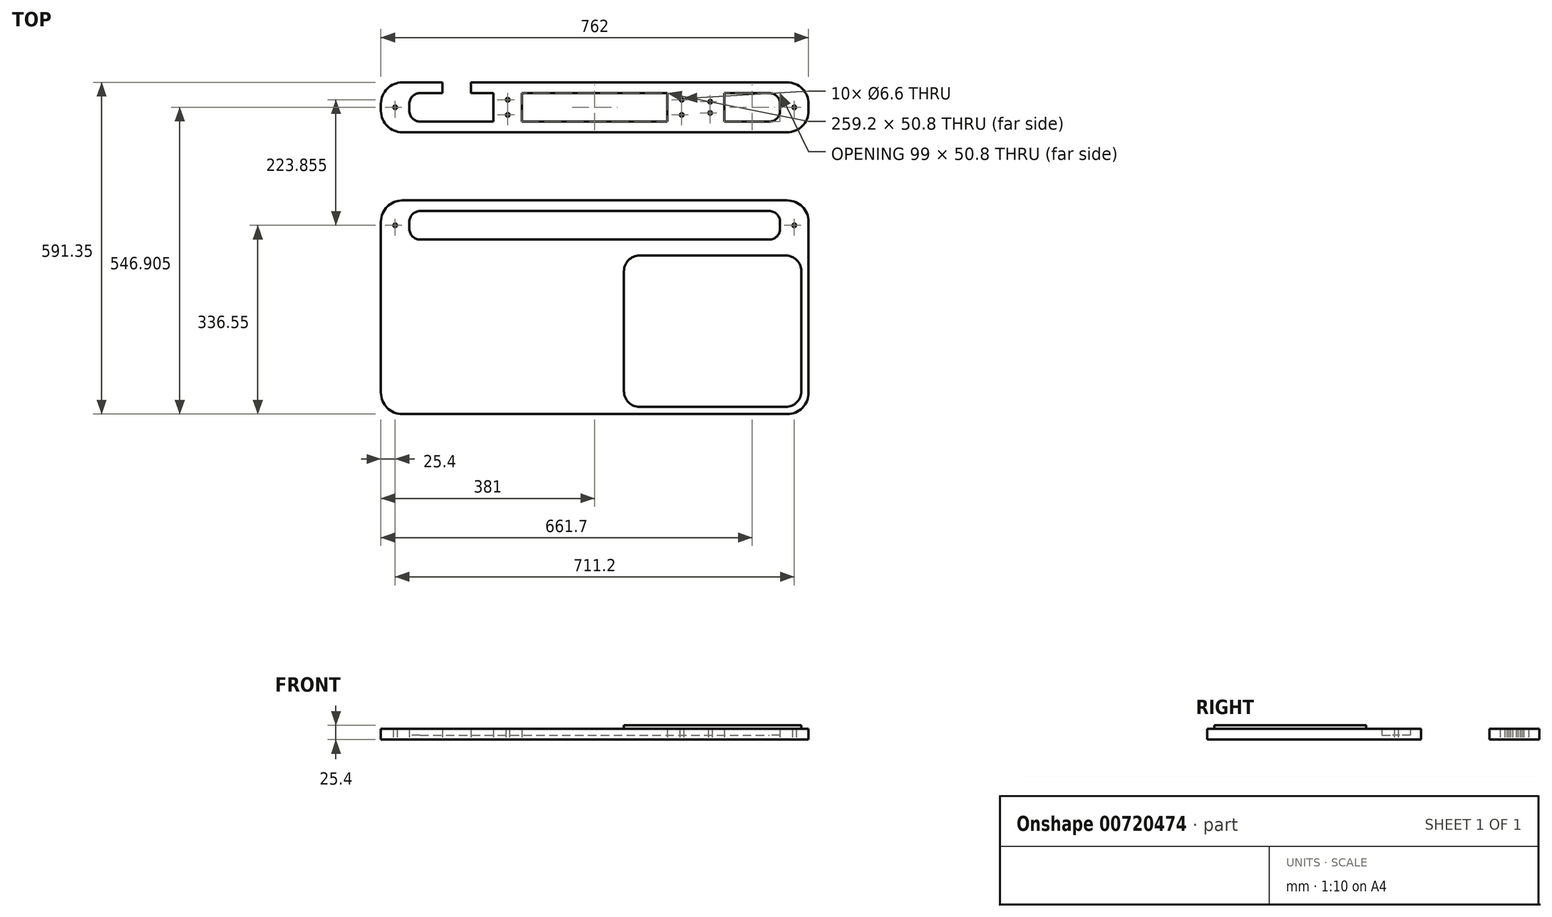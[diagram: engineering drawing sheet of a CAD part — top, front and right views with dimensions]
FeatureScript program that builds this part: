
annotation { "Feature Type Name" : "Feature", "Feature Type Description" : "" }
export const myFeature = defineFeature(function(context is Context, id is Id, definition is map)
    precondition{}
    {
        {
            var Q0;
            Q0=qCreatedBy(makeId("Top.planeOp"),FACE);
            var sketch = newSketch(context, id + "F0", { "sketchPlane" : qUnion([Q0])});
            skLineSegment(sketch, "E0.bottom", {"start": v(342.9, -190.5) * mm, "end": v(-342.9, -190.5) * mm});
            skLineSegment(sketch, "E0.top", {"start": v(342.9, 190.5) * mm, "end": v(-342.9, 190.5) * mm});
            skLineSegment(sketch, "E0.left", {"start": v(381, -152.4) * mm, "end": v(381, 152.4) * mm});
            skLineSegment(sketch, "E0.right", {"start": v(-381, -152.4) * mm, "end": v(-381, 152.4) * mm});
            skPoint(sketch, "E0.middle", {"position": v(0, 0) * mm});
            skLineSegment(sketch, "E1.bottom", {"start": v(340.3, -177.8) * mm, "end": v(80.07, -177.8) * mm});
            skLineSegment(sketch, "E1.top", {"start": v(340.3, 92.2) * mm, "end": v(80.07, 92.2) * mm});
            skLineSegment(sketch, "E1.left", {"start": v(368.3, -149.8) * mm, "end": v(368.3, 64.2) * mm});
            skLineSegment(sketch, "E1.right", {"start": v(52.07, -149.8) * mm, "end": v(52.07, 64.2) * mm});
            skPoint(sketch, "E1.middle", {"position": v(210.19, -42.8) * mm});
            skPoint(sketch, "E2.visualSharp", {"position": v(52.07, 92.2) * mm});
            skArc(sketch, "E2.filletArc", {"start": v(80.07, 92.2) * mm, "mid": v(60.27, 84) * mm, "end": v(52.07, 64.2) * mm});
            skPoint(sketch, "E3.visualSharp", {"position": v(368.3, 92.2) * mm});
            skArc(sketch, "E3.filletArc", {"start": v(368.3, 64.2) * mm, "mid": v(360.1, 84) * mm, "end": v(340.3, 92.2) * mm});
            skPoint(sketch, "E4.visualSharp", {"position": v(368.3, -177.8) * mm});
            skArc(sketch, "E4.filletArc", {"start": v(340.3, -177.8) * mm, "mid": v(360.1, -169.6) * mm, "end": v(368.3, -149.8) * mm});
            skPoint(sketch, "E5.visualSharp", {"position": v(52.07, -177.8) * mm});
            skArc(sketch, "E5.filletArc", {"start": v(52.07, -149.8) * mm, "mid": v(60.27, -169.6) * mm, "end": v(80.07, -177.8) * mm});
            skPoint(sketch, "E6.visualSharp", {"position": v(-381, 190.5) * mm});
            skArc(sketch, "E6.filletArc", {"start": v(-342.9, 190.5) * mm, "mid": v(-369.84, 179.34) * mm, "end": v(-381, 152.4) * mm});
            skPoint(sketch, "E7.visualSharp", {"position": v(-381, -190.5) * mm});
            skArc(sketch, "E7.filletArc", {"start": v(-381, -152.4) * mm, "mid": v(-369.84, -179.34) * mm, "end": v(-342.9, -190.5) * mm});
            skPoint(sketch, "E8.visualSharp", {"position": v(381, 190.5) * mm});
            skArc(sketch, "E8.filletArc", {"start": v(381, 152.4) * mm, "mid": v(369.84, 179.34) * mm, "end": v(342.9, 190.5) * mm});
            skPoint(sketch, "E9.visualSharp", {"position": v(381, -190.5) * mm});
            skArc(sketch, "E9.filletArc", {"start": v(342.9, -190.5) * mm, "mid": v(369.84, -179.34) * mm, "end": v(381, -152.4) * mm});
            skLineSegment(sketch, "E10", {"start": v(-342.9, 311.95) * mm, "end": v(342.9, 311.95) * mm});
            skLineSegment(sketch, "E11", {"start": v(381, 350.05) * mm, "end": v(381, 362.75) * mm});
            skLineSegment(sketch, "E12", {"start": v(-381, 350.05) * mm, "end": v(-381, 362.75) * mm});
            skLineSegment(sketch, "E13", {"start": v(-342.9, 400.85) * mm, "end": v(342.9, 400.85) * mm});
            skPoint(sketch, "E14.visualSharp", {"position": v(-381, 400.85) * mm});
            skArc(sketch, "E14.filletArc", {"start": v(-342.9, 400.85) * mm, "mid": v(-369.84, 389.7) * mm, "end": v(-381, 362.75) * mm});
            skPoint(sketch, "E15.visualSharp", {"position": v(381, 400.85) * mm});
            skArc(sketch, "E15.filletArc", {"start": v(381, 362.75) * mm, "mid": v(369.84, 389.7) * mm, "end": v(342.9, 400.85) * mm});
            skPoint(sketch, "E16.visualSharp", {"position": v(-381, 311.95) * mm});
            skArc(sketch, "E16.filletArc", {"start": v(-381, 350.05) * mm, "mid": v(-369.84, 323.11) * mm, "end": v(-342.9, 311.95) * mm});
            skPoint(sketch, "E17.visualSharp", {"position": v(381, 311.95) * mm});
            skArc(sketch, "E17.filletArc", {"start": v(342.9, 311.95) * mm, "mid": v(369.84, 323.11) * mm, "end": v(381, 350.05) * mm});
            skCircle(sketch, "E18", {"center": v(-355.6, 356.4) * mm, "radius": 3.3 * mm});
            skPoint(sketch, "E18.centerSnap0", {"position": v(-381, 356.4) * mm});
            skCircle(sketch, "E19", {"center": v(355.6, 356.4) * mm, "radius": 3.3 * mm});
            skPoint(sketch, "E19.centerSnap0", {"position": v(381, 356.4) * mm});
            skCircle(sketch, "E20", {"center": v(-355.6, 146.05) * mm, "radius": 3.3 * mm});
            skCircle(sketch, "E21", {"center": v(355.6, 146.05) * mm, "radius": 3.3 * mm});
            skLineSegment(sketch, "E22.bottom", {"start": v(-311.15, 171.45) * mm, "end": v(311.15, 171.45) * mm});
            skLineSegment(sketch, "E22.top", {"start": v(-311.15, 120.65) * mm, "end": v(311.15, 120.65) * mm});
            skLineSegment(sketch, "E22.left", {"start": v(-330.2, 152.4) * mm, "end": v(-330.2, 139.7) * mm});
            skLineSegment(sketch, "E22.right", {"start": v(330.2, 152.4) * mm, "end": v(330.2, 139.7) * mm});
            skPoint(sketch, "E23.visualSharp", {"position": v(-330.2, 381.8) * mm});
            skPoint(sketch, "E24.visualSharp", {"position": v(-330.2, 331) * mm});
            skPoint(sketch, "E25.visualSharp", {"position": v(330.2, 331) * mm});
            skPoint(sketch, "E26.visualSharp", {"position": v(330.2, 381.8) * mm});
            skPoint(sketch, "E27.visualSharp", {"position": v(-330.2, 171.45) * mm});
            skArc(sketch, "E27.filletArc", {"start": v(-311.15, 171.45) * mm, "mid": v(-324.62, 165.87) * mm, "end": v(-330.2, 152.4) * mm});
            skPoint(sketch, "E28.visualSharp", {"position": v(-330.2, 120.65) * mm});
            skArc(sketch, "E28.filletArc", {"start": v(-330.2, 139.7) * mm, "mid": v(-324.62, 126.23) * mm, "end": v(-311.15, 120.65) * mm});
            skPoint(sketch, "E29.visualSharp", {"position": v(330.2, 171.45) * mm});
            skArc(sketch, "E29.filletArc", {"start": v(330.2, 152.4) * mm, "mid": v(324.62, 165.87) * mm, "end": v(311.15, 171.45) * mm});
            skPoint(sketch, "E30.visualSharp", {"position": v(330.2, 120.65) * mm});
            skArc(sketch, "E30.filletArc", {"start": v(311.15, 120.65) * mm, "mid": v(324.62, 126.23) * mm, "end": v(330.2, 139.7) * mm});
            skLineSegment(sketch, "E31", {"start": v(-155, 381.8) * mm, "end": v(-155, 331) * mm});
            skCircle(sketch, "E32", {"center": v(-155, 369.9) * mm, "radius": 3.3 * mm});
            skCircle(sketch, "E33", {"center": v(-155, 342.9) * mm, "radius": 3.3 * mm});
            skCircle(sketch, "E34", {"center": v(155, 369.9) * mm, "radius": 3.3 * mm});
            skCircle(sketch, "E35", {"center": v(155, 342.9) * mm, "radius": 3.3 * mm});
            skCircle(sketch, "E36", {"center": v(205.8, 366.4) * mm, "radius": 3.3 * mm});
            skCircle(sketch, "E37", {"center": v(205.8, 346.4) * mm, "radius": 3.3 * mm});
            skLineSegment(sketch, "E38.bottom", {"start": v(-311.15, 381.8) * mm, "end": v(-180.4, 381.8) * mm});
            skLineSegment(sketch, "E38.top", {"start": v(-311.15, 331) * mm, "end": v(-180.4, 331) * mm});
            skLineSegment(sketch, "E38.left", {"start": v(-330.2, 362.75) * mm, "end": v(-330.2, 350.05) * mm});
            skLineSegment(sketch, "E38.right", {"start": v(-180.4, 381.8) * mm, "end": v(-180.4, 331) * mm});
            skArc(sketch, "E39.filletArc", {"start": v(-311.15, 381.8) * mm, "mid": v(-324.62, 376.23) * mm, "end": v(-330.2, 362.75) * mm});
            skArc(sketch, "E40.filletArc", {"start": v(-330.2, 350.05) * mm, "mid": v(-324.62, 336.58) * mm, "end": v(-311.15, 331) * mm});
            skLineSegment(sketch, "E41.bottom", {"start": v(-129.6, 381.8) * mm, "end": v(129.6, 381.8) * mm});
            skLineSegment(sketch, "E41.top", {"start": v(-129.6, 331) * mm, "end": v(129.6, 331) * mm});
            skLineSegment(sketch, "E41.left", {"start": v(-129.6, 381.8) * mm, "end": v(-129.6, 331) * mm});
            skLineSegment(sketch, "E41.right", {"start": v(129.6, 381.8) * mm, "end": v(129.6, 331) * mm});
            skLineSegment(sketch, "E42.bottom", {"start": v(231.2, 381.8) * mm, "end": v(311.15, 381.8) * mm});
            skLineSegment(sketch, "E42.top", {"start": v(231.2, 331) * mm, "end": v(311.15, 331) * mm});
            skLineSegment(sketch, "E42.left", {"start": v(231.2, 381.8) * mm, "end": v(231.2, 331) * mm});
            skLineSegment(sketch, "E42.right", {"start": v(330.2, 362.75) * mm, "end": v(330.2, 350.05) * mm});
            skArc(sketch, "E43.filletArc", {"start": v(330.2, 362.75) * mm, "mid": v(324.62, 376.23) * mm, "end": v(311.15, 381.8) * mm});
            skArc(sketch, "E44.filletArc", {"start": v(311.15, 331) * mm, "mid": v(324.62, 336.58) * mm, "end": v(330.2, 350.05) * mm});
            skLineSegment(sketch, "E45.bottom", {"start": v(-220.38, 355.17) * mm, "end": v(-271.18, 355.17) * mm});
            skLineSegment(sketch, "E45.top", {"start": v(-220.38, 408.44) * mm, "end": v(-271.18, 408.44) * mm});
            skLineSegment(sketch, "E45.left", {"start": v(-220.38, 355.17) * mm, "end": v(-220.38, 408.44) * mm});
            skLineSegment(sketch, "E45.right", {"start": v(-271.18, 355.17) * mm, "end": v(-271.18, 408.44) * mm});
            skPoint(sketch, "E45.middle", {"position": v(-245.78, 381.8) * mm});
            skPoint(sketch, "E46", {"position": v(-271.18, 400.85) * mm});
            skSolve(sketch);
        }
        {
            var Q0;
            Q0=makeQuery(id+"F0.imprint","IMPRINT",FACE,{"disambiguationData":[TD([[makeQuery(id+"F0.imprint","IMPRINT",EDGE,{"derivedFrom":sQuery(id+"F0.wireOp",EDGE,"E10")}),1.0]])]});
            var Q1;
            {var subQ7=sQuery(id+"F0.wireOp",EDGE,"H69vqx1G-RbOf-b5aH-RZhy-8KIsay9wq3rC");Q1=makeQuery(id+"F0.imprint","IMPRINT",FACE,{"disambiguationData":[TD([[makeQuery(id+"F0.imprint","IMPRINT",EDGE,{"derivedFrom":subQ7}),1.0]])]});}
            var Q2;
            {var subQ9=sQuery(id+"F0.wireOp",EDGE,"E7D3JbQL-pDhf-WXmA-9WqY-JGjtphdddMJD");Q2=makeQuery(id+"F0.imprint","IMPRINT",FACE,{"disambiguationData":[TD([[makeQuery(id+"F0.imprint","IMPRINT",EDGE,{"derivedFrom":subQ9}),-1.0]])]});}
            var Q3;
            {var subQ0=sQuery(id+"F0.wireOp",EDGE,"WLNJXWbx-ADK6-wmOS-BF5h-tdosZukIXvz6");Q3=makeQuery(id+"F0.imprint","IMPRINT",FACE,{"disambiguationData":[TD([[makeQuery(id+"F0.imprint","IMPRINT",EDGE,{"derivedFrom":subQ0}),-1.0]])]});}
            var Q4;
            {var subQ0=sQuery(id+"F0.wireOp",EDGE,"WLNJXWbx-ADK6-wmOS-BF5h-tdosZukIXvz6");Q4=makeQuery(id+"F0.imprint","IMPRINT",FACE,{"disambiguationData":[TD([[makeQuery(id+"F0.imprint","IMPRINT",EDGE,{"derivedFrom":subQ0}),1.0]])]});}
            extrude(context, id + "F1", {"entities" : qUnion([Q0, Q1, Q2, Q3, Q4]), "depth" : 19.05 * mm, "offsetDistance" : 25.4 * mm});
        }
        {
            var Q0;
            Q0=makeQuery(id+"F0.imprint","IMPRINT",FACE,{"disambiguationData":[TD([[makeQuery(id+"F0.imprint","IMPRINT",EDGE,{"derivedFrom":sQuery(id+"F0.wireOp",EDGE,"E0.bottom")}),-1.0]])]});
            var Q1;
            Q1=makeQuery(id+"F0.imprint","IMPRINT",FACE,{"disambiguationData":[TD([[makeQuery(id+"F0.imprint","IMPRINT",EDGE,{"derivedFrom":sQuery(id+"F0.wireOp",EDGE,"E1.bottom")}),-1.0]])]});
            extrude(context, id + "F2", {"entities" : qUnion([Q0, Q1]), "depth" : 19.05 * mm, "offsetDistance" : 25.4 * mm});
        }
        {
            var Q0;
            Q0=makeQuery(id+"F0.imprint","IMPRINT",FACE,{"disambiguationData":[TD([[makeQuery(id+"F0.imprint","IMPRINT",EDGE,{"derivedFrom":sQuery(id+"F0.wireOp",EDGE,"E22.bottom")}),-1.0]])]});
            extrude(context, id + "F3", {"entities" : qUnion([Q0]), "operationType" : NewBodyOperationType.ADD, "depth" : 7.62 * mm, "offsetDistance" : 25.4 * mm});
        }
        {
            var Q0;
            Q0=makeQuery(id+"F0.imprint","IMPRINT",FACE,{"disambiguationData":[TD([[makeQuery(id+"F0.imprint","IMPRINT",EDGE,{"derivedFrom":sQuery(id+"F0.wireOp",EDGE,"E1.bottom")}),-1.0]])]});
            extrude(context, id + "F4", {"entities" : qUnion([Q0]), "operationType" : NewBodyOperationType.ADD, "depth" : 25.4 * mm, "offsetDistance" : 25.4 * mm});
        }
    });
